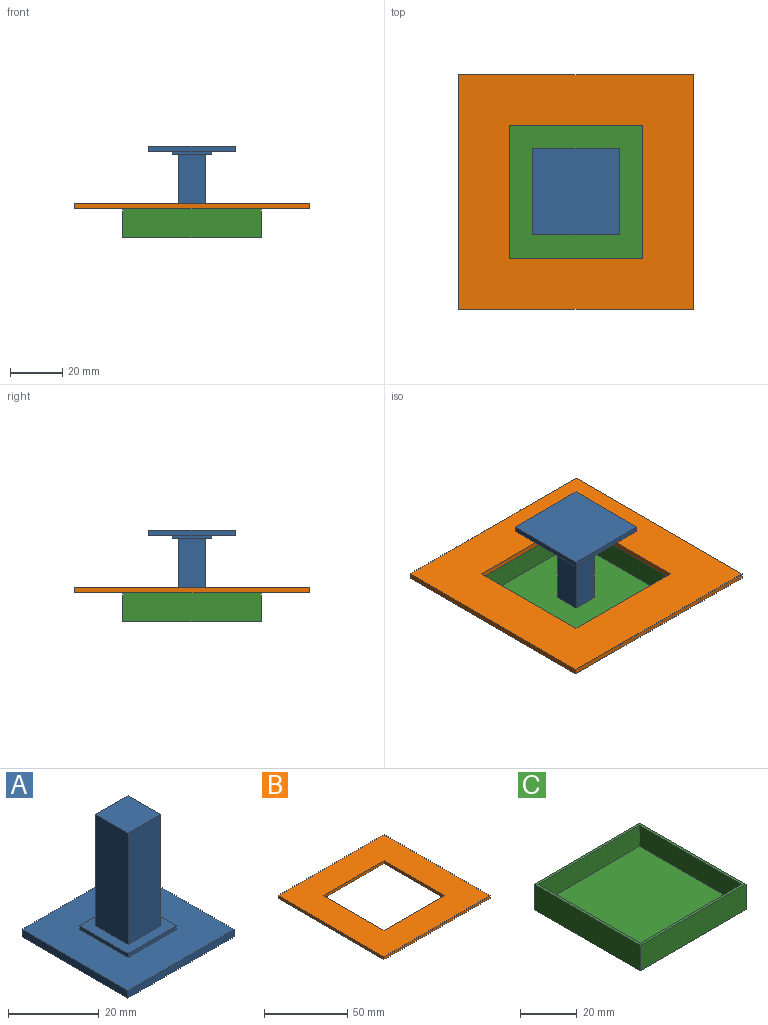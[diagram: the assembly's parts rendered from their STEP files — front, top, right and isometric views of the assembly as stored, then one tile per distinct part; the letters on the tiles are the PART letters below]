
ASSEMBLY  parts=3 mates=4
PART A: 16 faces, bbox 33x33x33 mm
  f0: plane 15x15mm, normal (0,0,1), area 125mm2, adj f7,f8,f9,f10,f11,f12,f13,f14
  f1: plane 33x33mm, normal (0,0,1), area 864mm2, adj f2,f3,f4,f5,f7,f8,f9,f10
  f2: plane 33x2mm, normal (0,-1,0), area 66mm2, adj f1,f3,f5,f6
  f3: plane 33x2mm, normal (1,0,0), area 66mm2, adj f1,f2,f4,f6
  f4: plane 33x2mm, normal (0,1,0), area 66mm2, adj f1,f3,f5,f6
  f5: plane 33x2mm, normal (-1,0,0), area 66mm2, adj f1,f2,f4,f6
  f6: plane 33x33mm, normal (0,0,-1), area 1089mm2, adj f2,f3,f4,f5
  f7: plane 15x1mm, normal (0,-1,0), area 15mm2, adj f0,f1,f8,f10
  f8: plane 15x1mm, normal (1,0,0), area 15mm2, adj f0,f1,f7,f9
  f9: plane 15x1mm, normal (0,1,0), area 15mm2, adj f0,f1,f8,f10
  f10: plane 15x1mm, normal (-1,0,0), area 15mm2, adj f0,f1,f7,f9
  f11: plane 30x10mm, normal (0,-1,0), area 300mm2, adj f0,f12,f14,f15
  f12: plane 30x10mm, normal (1,0,0), area 300mm2, adj f0,f11,f13,f15
  f13: plane 30x10mm, normal (0,1,0), area 300mm2, adj f0,f12,f14,f15
  f14: plane 30x10mm, normal (-1,0,0), area 300mm2, adj f0,f11,f13,f15
  f15: plane 10x10mm, normal (0,0,1), area 100mm2, adj f11,f12,f13,f14
PART B: 10 faces, bbox 90x90x2 mm
  f0: plane 90x2mm, normal (0,-1,0), area 180mm2, adj f1,f7,f8,f9
  f1: plane 90x2mm, normal (1,0,0), area 180mm2, adj f0,f2,f8,f9
  f2: plane 90x2mm, normal (0,1,0), area 180mm2, adj f1,f7,f8,f9
  f3: plane 51x2mm, normal (-1,0,0), area 102mm2, adj f4,f6,f8,f9
  f4: plane 51x2mm, normal (0,1,0), area 102mm2, adj f3,f5,f8,f9
  f5: plane 51x2mm, normal (1,0,0), area 102mm2, adj f4,f6,f8,f9
  f6: plane 51x2mm, normal (0,-1,0), area 102mm2, adj f3,f5,f8,f9
  f7: plane 90x2mm, normal (-1,0,0), area 180mm2, adj f0,f2,f8,f9
  f8: plane 90x90mm, normal (0,0,1), area 5499mm2, adj f0,f1,f2,f3,f4,f5,f6,f7
  f9: plane 90x90mm, normal (0,0,-1), area 5499mm2, adj f0,f1,f2,f3,f4,f5,f6,f7
PART C: 16 faces, bbox 53x53x11 mm
  f0: plane 53x11mm, normal (0,-1,0), area 583mm2, adj f1,f3,f4,f9
  f1: plane 53x11mm, normal (1,0,0), area 583mm2, adj f0,f2,f4,f9
  f2: plane 53x11mm, normal (0,1,0), area 583mm2, adj f1,f3,f4,f9
  f3: plane 53x11mm, normal (-1,0,0), area 583mm2, adj f0,f2,f4,f9
  f4: plane 53x53mm, normal (0,0,1), area 208mm2, adj f0,f1,f2,f3,f11,f12,f13,f14
  f5: plane 51x1mm, normal (-1,0,0), area 51mm2, adj f6,f8,f9,f10
  f6: plane 51x1mm, normal (0,-1,0), area 51mm2, adj f5,f7,f9,f10
  f7: plane 51x1mm, normal (1,0,0), area 51mm2, adj f6,f8,f9,f10
  f8: plane 51x1mm, normal (0,1,0), area 51mm2, adj f5,f7,f9,f10
  f9: plane 53x53mm, normal (0,0,-1), area 208mm2, adj f0,f1,f2,f3,f5,f6,f7,f8
  f10: plane 51x51mm, normal (0,0,-1), area 2601mm2, adj f5,f6,f7,f8
  f11: plane 51x9mm, normal (0,1,0), area 459mm2, adj f4,f12,f14,f15
  f12: plane 51x9mm, normal (-1,0,0), area 459mm2, adj f4,f11,f13,f15
  f13: plane 51x9mm, normal (0,-1,0), area 459mm2, adj f4,f12,f14,f15
  f14: plane 51x9mm, normal (1,0,0), area 459mm2, adj f4,f11,f13,f15
  f15: plane 51x51mm, normal (0,0,1), area 2601mm2, adj f11,f12,f13,f14
PLACE A rot(axis=(1,0,0),180deg) t=(6.38,-9.37,47.59)mm
PLACE B t=(6.38,-9.37,23.59)mm
PLACE C t=(6.38,-9.37,13.59)mm
MATE planar B.f3 <-> C.f12  axis (-1,0,0) through (31.88,-9.37,24.59)mm
MATE planar A.f15 <-> C.f15  axis (0,0,-1) through (6.38,-9.37,14.59)mm
MATE planar B.f6 <-> C.f13  axis (0,-1,0) through (6.38,16.13,24.59)mm
MATE planar C.f4 <-> B.f9  axis (0,0,1) through (-19.12,-34.87,23.59)mm
